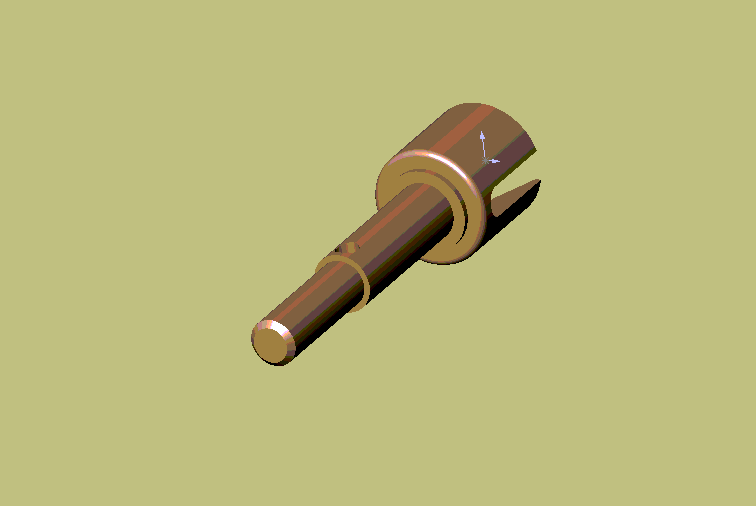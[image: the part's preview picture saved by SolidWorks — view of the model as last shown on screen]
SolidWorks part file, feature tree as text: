
SOLIDWORKS PART (.sldprt)
format: sldprt  version: not decoded by parser v0  size: 194,048 bytes
history: native  units: mm
features: sketch x7, extrude x4, plane x3, cut_extrude x2, material x1, chamfer x1, fillet x1, cut_revolve x1 (+8 scaffold rows collapsed)
feature tree (28):
  scaffold x8  (default folders/planes/origin — collapsed)
  material  "Matériau <non spécifié>"
  plane  "Plane1"
  plane  "Plane2"
  plane  "Plane3"
  sketch  "Esquisse1"  dims[D1=10.0mm]
  extrude  "Base-Extrusion"  Depth=9.5mm
  sketch  "Esquisse2"  dims[D1=7.0mm]
  extrude  "Boss.-Extru.1"  Depth=0.5mm
  sketch  "Esquisse3"  dims[D1=5.0mm]
  extrude  "Boss.-Extru.2"  Depth=14mm
  sketch  "Esquisse4"  dims[D1=4.0mm]
  extrude  "Boss.-Extru.3"  Depth=12mm
  chamfer  "Chanfrein1"  Distance=0.5mm Angle=45deg
  fillet  "Congé1"  Radius=0.5mm
  sketch  "Esquisse7"  dims[D1=7.0mm D2=2.5mm]
  cut_extrude  "Enlèv. mat.-Extru.1"  Depth=32mm
  sketch  "Esquisse8"  dims[D1=4.0mm D2=3.0mm D3=4.0mm D4=1.5mm D5=4.5mm]
  cut_revolve  "Enlèvement de matière-Révolution1"  Angle=360deg
  sketch  "Esquisse9"  dims[D1=2.0mm D2=12.5mm]
  cut_extrude  "Enlèv. mat.-Extru.2"  Depth=20mm
decode coverage: 16 of 16 modeling features carry decoded parameters
note: suppression state not decoded; provenance and decode notes live in map.json
